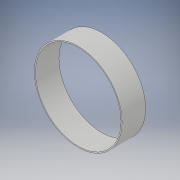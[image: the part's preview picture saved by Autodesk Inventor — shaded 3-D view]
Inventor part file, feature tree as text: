
AUTODESK INVENTOR PART (.ipt)
format: ipt  version: 2019 (Build 230136000, 136)  size: 105,472 bytes
history: native  units: mm
features: extrude x2, sketch x2
ambient origin geometry x8: Origin, YZ Plane, XZ Plane, XY Plane, X Axis, Y Axis, Z Axis, Center Point
bodies: Solid1 (feature_tree)
feature tree (4):
  extrude  "Extrusion1"  Depth=116.5mm TaperAngle=0.0deg
  extrude  "Extrusion2"  Depth=11.65mm TaperAngle=0.0deg
  sketch  "Sketch1"  dims[d0=434.0mm d1=116.5mm d2=0.0mm]
  sketch  "Sketch2"  dims[d3=424.0mm d4=11.65mm d5=0.0mm]
